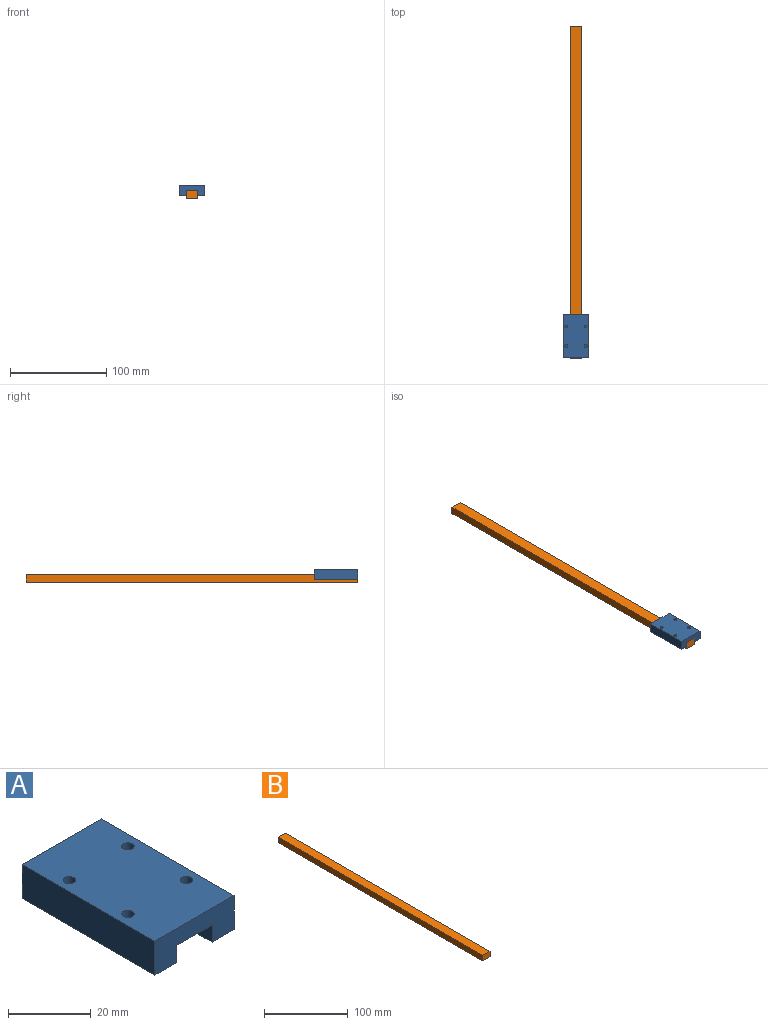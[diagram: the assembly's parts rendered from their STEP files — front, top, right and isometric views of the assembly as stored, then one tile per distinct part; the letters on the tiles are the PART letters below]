
ASSEMBLY  parts=2 mates=1
PART A: 18 faces, bbox 27x45.4x10 mm
  f0: plane 45.4x7.5mm, normal (0,0,-1), area 340.5mm2, adj f1,f7,f8,f9
  f1: plane 45.4x5mm, normal (1,0,0), area 227mm2, adj f0,f2,f8,f9
  f2: plane 45.4x12mm, normal (0,0,-1), area 544.8mm2, adj f1,f3,f8,f9
  f3: plane 45.4x5mm, normal (-1,0,0), area 227mm2, adj f2,f4,f8,f9
  f4: plane 45.4x7.5mm, normal (0,0,-1), area 340.5mm2, adj f3,f5,f8,f9
  f5: plane 45.4x10mm, normal (1,0,0), area 454mm2, adj f4,f6,f8,f9
  f6: plane 45.4x27mm, normal (0,0,1), area 1197.5mm2, adj f5,f7,f8,f9,f10,f12,f14,f16
  f7: plane 45.4x10mm, normal (-1,0,0), area 454mm2, adj f0,f6,f8,f9
  f8: plane 27x10mm, normal (0,-1,0), area 210mm2, adj f0,f1,f2,f3,f4,f5,f6,f7
  f9: plane 27x10mm, normal (0,1,0), area 210mm2, adj f0,f1,f2,f3,f4,f5,f6,f7
  f10: cylinder r=1.5mm len=3.5mm, axis (0,0,1), area 33mm2, adj f6,f11
  f11: plane 3x3mm, normal (0,0,1), area 7.1mm2, adj f10
  f12: cylinder r=1.5mm len=3.5mm, axis (0,0,1), area 33mm2, adj f6,f13
  f13: plane 3x3mm, normal (0,0,1), area 7.1mm2, adj f12
  f14: cylinder r=1.5mm len=3.5mm, axis (0,0,1), area 33mm2, adj f6,f15
  f15: plane 3x3mm, normal (0,0,1), area 7.1mm2, adj f14
  f16: cylinder r=1.5mm len=3.5mm, axis (0,0,1), area 33mm2, adj f6,f17
  f17: plane 3x3mm, normal (0,0,1), area 7.1mm2, adj f16
PART B: 6 faces, bbox 12x345x8 mm
  f0: plane 345x12mm, normal (0,0,-1), area 4140mm2, adj f1,f3,f4,f5
  f1: plane 345x8mm, normal (1,0,0), area 2760mm2, adj f0,f2,f4,f5
  f2: plane 345x12mm, normal (0,0,1), area 4140mm2, adj f1,f3,f4,f5
  f3: plane 345x8mm, normal (-1,0,0), area 2760mm2, adj f0,f2,f4,f5
  f4: plane 12x8mm, normal (0,-1,0), area 96mm2, adj f0,f1,f2,f3
  f5: plane 12x8mm, normal (0,1,0), area 96mm2, adj f0,f1,f2,f3
PLACE A t=(0,-127.1,8)mm
PLACE B t=(0,0,4)mm
MATE slider B.f4 <-> A.f8  axis (0,-1,0) through (-6,-172.5,8)mm
